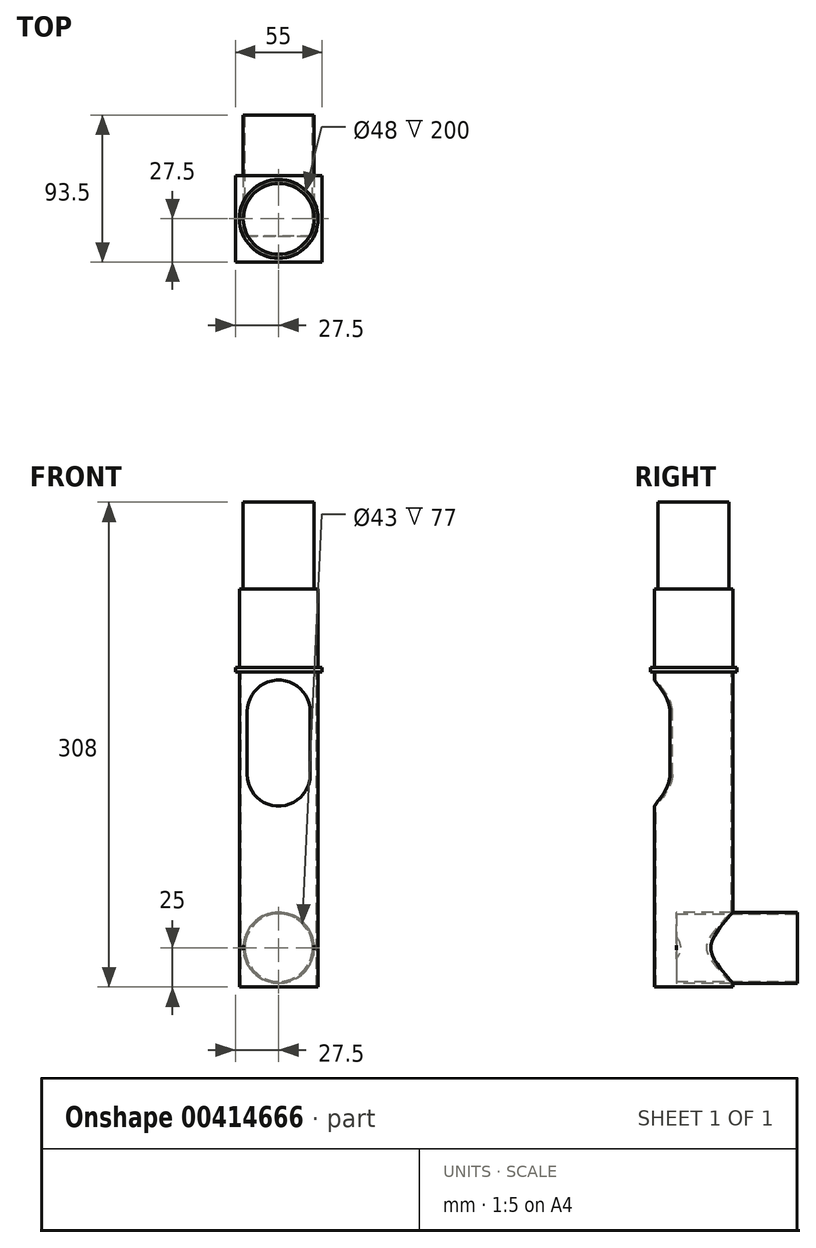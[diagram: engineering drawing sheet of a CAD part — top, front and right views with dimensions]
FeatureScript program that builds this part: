
annotation { "Feature Type Name" : "Feature", "Feature Type Description" : "" }
export const myFeature = defineFeature(function(context is Context, id is Id, definition is map)
    precondition{}
    {
        {
            var Q0;
            Q0=qCreatedBy(makeId("Right.planeOp"),FACE);
            var sketch = newSketch(context, id + "F0", { "sketchPlane" : qUnion([Q0])});
            skLineSegment(sketch, "E0", {"start": v(0, 0) * mm, "end": v(0, 200) * mm});
            skSolve(sketch);
        }
        {
            var Q0;
            Q0=qCreatedBy(makeId("Top.planeOp"),FACE);
            var sketch = newSketch(context, id + "F1", { "sketchPlane" : qUnion([Q0])});
            skCircle(sketch, "E1", {"center": v(0, 0) * mm, "radius": 25 * mm});
            skCircle(sketch, "E2.0", {"center": v(0, 0) * mm, "radius": 24 * mm});
            skSolve(sketch);
        }
        {
            var Q0;
            Q0=makeQuery(id+"F1.imprint","IMPRINT",FACE,{"disambiguationData":[TD([[makeQuery(id+"F1.imprint","IMPRINT",EDGE,{"derivedFrom":sQuery(id+"F1.wireOp",EDGE,"E1")}),1.0]])]});
            var Q1;
            Q1=sQuery(id+"F0.wireOp",EDGE,"E0");
            sweep(context, id + "F2", {"profiles" : qUnion([Q0]), "path" : qUnion([Q1])});
        }
        {
            var Q0;
            Q0=qCreatedBy(makeId("Right.planeOp"),FACE);
            var sketch = newSketch(context, id + "F3", { "sketchPlane" : qUnion([Q0])});
            skLineSegment(sketch, "E3.0", {"start": v(-25, 200) * mm, "end": v(25, 200) * mm});
            skLineSegment(sketch, "E4.bottom", {"start": v(-27.5, 200) * mm, "end": v(27.5, 200) * mm});
            skLineSegment(sketch, "E4.top", {"start": v(-27.5, 203) * mm, "end": v(27.5, 203) * mm});
            skLineSegment(sketch, "E4.left", {"start": v(-27.5, 200) * mm, "end": v(-27.5, 203) * mm});
            skLineSegment(sketch, "E4.right", {"start": v(27.5, 200) * mm, "end": v(27.5, 203) * mm});
            skLineSegment(sketch, "E5", {"start": v(0, 646.95) * mm, "end": v(0, 656.05) * mm, "construction": true});
            skPoint(sketch, "E5.endSnap0", {"position": v(0, 200) * mm});
            skSolve(sketch);
        }
        {
            var Q0;
            Q0=makeQuery(id+"F3.imprint","IMPRINT",FACE,{"disambiguationData":[TD([[makeQuery(id+"F3.imprint","IMPRINT",EDGE,{"derivedFrom":sQuery(id+"F3.wireOp",EDGE,"E4.top")}),-1.0]])]});
            extrude(context, id + "F4", {"entities" : qUnion([Q0]), "operationType" : NewBodyOperationType.ADD, "endBound" : BoundingType.SYMMETRIC, "depth" : 55 * mm});
        }
        {
            var Q0;
            Q0=makeQuery(id+"F4.opExtrude","SWEPT_FACE",FACE,{"disambiguationData":[OSD([sQuery(id+"F3.wireOp",EDGE,"E4.top")])]});
            var sketch = newSketch(context, id + "F5", { "sketchPlane" : qUnion([Q0])});
            skCircle(sketch, "E6", {"center": v(0, 0) * mm, "radius": 25 * mm});
            skSolve(sketch);
        }
        {
            var Q0;
            Q0=qSketchRegion(id+"F5",true);
            extrude(context, id + "F6", {"entities" : qUnion([Q0]), "operationType" : NewBodyOperationType.ADD, "depth" : 50 * mm});
        }
        {
            var Q0;
            Q0=makeQuery(id+"F6.opExtrude","CAP_FACE",FACE,{"disambiguationData":[OSD([sQuery(id+"F5.wireOp",EDGE,"E6")])],"isStart":false});
            var sketch = newSketch(context, id + "F7", { "sketchPlane" : qUnion([Q0])});
            skCircle(sketch, "E7", {"center": v(0, 0) * mm, "radius": 22.5 * mm});
            skSolve(sketch);
        }
        {
            var Q0;
            Q0=qSketchRegion(id+"F7",true);
            extrude(context, id + "F8", {"entities" : qUnion([Q0]), "operationType" : NewBodyOperationType.ADD, "depth" : 55 * mm});
        }
        {
            var Q0;
            Q0=makeQuery(id+"F4.opExtrude","SWEPT_FACE",FACE,{"disambiguationData":[OSD([sQuery(id+"F3.wireOp",EDGE,"E4.right")])]});
            var sketch = newSketch(context, id + "F9", { "sketchPlane" : qUnion([Q0])});
            skCircle(sketch, "E8", {"center": v(0, 25) * mm, "radius": 22.5 * mm});
            skCircle(sketch, "E9.0", {"center": v(0, 25) * mm, "radius": 21.5 * mm});
            skSolve(sketch);
        }
        {
            var Q0;
            Q0=makeQuery(id+"F9.imprint","IMPRINT",FACE,{"disambiguationData":[TD([[makeQuery(id+"F9.imprint","IMPRINT",EDGE,{"derivedFrom":sQuery(id+"F9.wireOp",EDGE,"E9.0")}),1.0]])]});
            extrude(context, id + "F10", {"entities" : qUnion([Q0]), "operationType" : NewBodyOperationType.REMOVE, "oppositeDirection" : true, "depth" : 20 * mm});
        }
        {
            var Q0;
            Q0=makeQuery(id+"F9.imprint","IMPRINT",FACE,{"disambiguationData":[TD([[makeQuery(id+"F9.imprint","IMPRINT",EDGE,{"derivedFrom":sQuery(id+"F9.wireOp",EDGE,"E8")}),1.0]])]});
            extrude(context, id + "F11", {"entities" : qUnion([Q0]), "operationType" : NewBodyOperationType.ADD, "endBound" : BoundingType.SYMMETRIC, "depth" : 77 * mm});
        }
        {
            var Q0;
            Q0=makeQuery(id+"F4.opExtrude","SWEPT_FACE",FACE,{"disambiguationData":[OSD([sQuery(id+"F3.wireOp",EDGE,"E4.left")])]});
            var sketch = newSketch(context, id + "F12", { "sketchPlane" : qUnion([Q0])});
            skLineSegment(sketch, "E10", {"start": v(25, 240.8) * mm, "end": v(25, 0) * mm});
            skLineSegment(sketch, "E11", {"start": v(-25, 0) * mm, "end": v(-25, 223.53) * mm});
            skArc(sketch, "E12", {"start": v(-20, 135) * mm, "mid": v(0, 115) * mm, "end": v(20, 135) * mm});
            skArc(sketch, "E13", {"start": v(20, 175) * mm, "mid": v(0, 195) * mm, "end": v(-20, 175) * mm});
            skLineSegment(sketch, "E14", {"start": v(-20, 175) * mm, "end": v(-20, 135) * mm});
            skLineSegment(sketch, "E15", {"start": v(20, 175) * mm, "end": v(20, 135) * mm});
            skSolve(sketch);
        }
        {
            var Q0;
            Q0=qSketchRegion(id+"F12",true);
            extrude(context, id + "F13", {"entities" : qUnion([Q0]), "operationType" : NewBodyOperationType.REMOVE, "oppositeDirection" : true, "depth" : (77 / 2) * mm});
        }
    });
